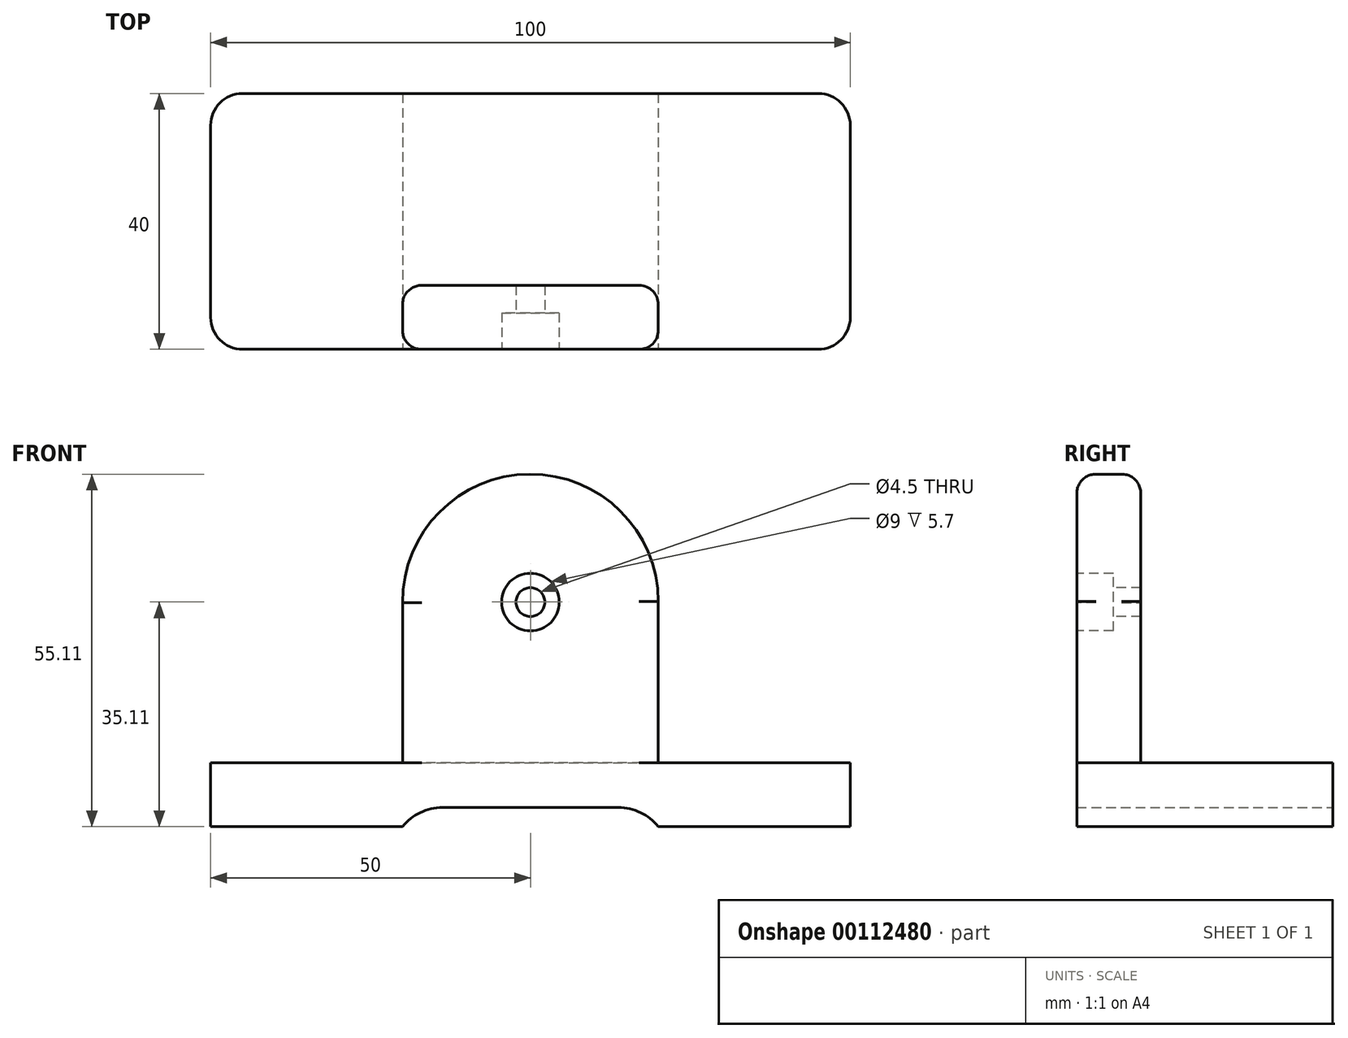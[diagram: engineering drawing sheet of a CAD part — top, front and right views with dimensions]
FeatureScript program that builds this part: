
annotation { "Feature Type Name" : "Feature", "Feature Type Description" : "" }
export const myFeature = defineFeature(function(context is Context, id is Id, definition is map)
    precondition{}
    {
        {
            var Q0;
            Q0=qCreatedBy(makeId("Top.planeOp"),FACE);
            var sketch = newSketch(context, id + "F0", { "sketchPlane" : qUnion([Q0])});
            skLineSegment(sketch, "E0.bottom", {"start": v(0, 0) * mm, "end": v(-100, 0) * mm});
            skLineSegment(sketch, "E0.top", {"start": v(0, 40) * mm, "end": v(-100, 40) * mm});
            skLineSegment(sketch, "E0.left", {"start": v(0, 0) * mm, "end": v(0, 40) * mm});
            skLineSegment(sketch, "E0.right", {"start": v(-100, 0) * mm, "end": v(-100, 40) * mm});
            skSolve(sketch);
        }
        {
            var Q0;
            Q0 = qSketchRegion(id + "F0", true);
            var Q1;
            Q1 = qSketchRegion(id + "F2", true);
            extrude(context, id + "F1", {"entities" : qUnion([Q0, Q1]), "depth" : 10 * mm});
        }
        {
            var Q0;
            Q0=qCreatedBy(makeId("Front.planeOp"),FACE);
            var sketch = newSketch(context, id + "F2", { "sketchPlane" : qUnion([Q0])});
            skLineSegment(sketch, "E1", {"start": v(-70, 35) * mm, "end": v(-70, 0) * mm});
            skLineSegment(sketch, "E2", {"start": v(-30, 0) * mm, "end": v(-30, 35.22) * mm});
            skArc(sketch, "E3", {"start": v(-30, 35.22) * mm, "mid": v(-50.1, 55.1) * mm, "end": v(-70, 35) * mm});
            skLineSegment(sketch, "E4", {"start": v(-70, 0) * mm, "end": v(-30, 0) * mm});
            skSolve(sketch);
        }
        {
            var Q0;
            Q0=makeQuery(id+"F2.imprint","IMPRINT",FACE,{"disambiguationData":[TD([[makeQuery(id+"F2.imprint","IMPRINT",EDGE,{"derivedFrom":sQuery(id+"F2.wireOp",EDGE,"E1")}),1.0]])]});
            extrude(context, id + "F3", {"entities" : qUnion([Q0]), "operationType" : NewBodyOperationType.ADD, "oppositeDirection" : true, "depth" : 10 * mm});
        }
        {
            var Q0;
            Q0=makeQuery(id+"F3.boolean.opBoolean","MERGE",FACE,{"derivedFrom":[makeQuery(id+"F1.opExtrude","SWEPT_FACE",FACE,{"disambiguationData":[OSD([sQuery(id+"F0.wireOp",EDGE,"E0.bottom")])]}),makeQuery(id+"F3.opExtrude","CAP_FACE",FACE,{"disambiguationData":[OSD([sQuery(id+"F2.wireOp",EDGE,"E1"),sQuery(id+"F2.wireOp",EDGE,"E2"),sQuery(id+"F2.wireOp",EDGE,"E3"),sQuery(id+"F2.wireOp",EDGE,"E4")])],"isStart":true})]});
            var sketch = newSketch(context, id + "F4", { "sketchPlane" : qUnion([Q0])});
            skLineSegment(sketch, "E5.bottom", {"start": v(-70, 0) * mm, "end": v(-30, 0) * mm});
            skLineSegment(sketch, "E5.top", {"start": v(-70, 3) * mm, "end": v(-30, 3) * mm});
            skLineSegment(sketch, "E5.left", {"start": v(-70, 0) * mm, "end": v(-70, 3) * mm});
            skLineSegment(sketch, "E5.right", {"start": v(-30, 0) * mm, "end": v(-30, 3) * mm});
            skSolve(sketch);
        }
        {
            var Q0;
            Q0 = qSketchRegion(id + "F4", true);
            extrude(context, id + "F5", {"entities" : qUnion([Q0]), "operationType" : NewBodyOperationType.REMOVE, "endBound" : BoundingType.THROUGH_ALL, "oppositeDirection" : true, "depth" : 25 * mm});
        }
        {
            var Q0;
            Q0=makeQuery(id+"F3.boolean.opBoolean","MERGE",FACE,{"derivedFrom":[makeQuery(id+"F1.opExtrude","SWEPT_FACE",FACE,{"disambiguationData":[OSD([sQuery(id+"F0.wireOp",EDGE,"E0.bottom")])]}),makeQuery(id+"F3.opExtrude","CAP_FACE",FACE,{"disambiguationData":[OSD([sQuery(id+"F2.wireOp",EDGE,"E1"),sQuery(id+"F2.wireOp",EDGE,"E2"),sQuery(id+"F2.wireOp",EDGE,"E3"),sQuery(id+"F2.wireOp",EDGE,"E4")])],"isStart":true})]});
            var sketch = newSketch(context, id + "F6", { "sketchPlane" : qUnion([Q0])});
            skCircle(sketch, "E6", {"center": v(-50, 35.1) * mm, "radius": 2.25 * mm});
            skSolve(sketch);
        }
        {
            var Q0;
            Q0 = qSketchRegion(id + "F6", true);
            extrude(context, id + "F7", {"entities" : qUnion([Q0]), "operationType" : NewBodyOperationType.REMOVE, "endBound" : BoundingType.THROUGH_ALL, "oppositeDirection" : true, "depth" : 25 * mm});
        }
        {
            var Q0;
            Q0=makeQuery(id+"F3.boolean.opBoolean","MERGE",FACE,{"derivedFrom":[makeQuery(id+"F1.opExtrude","SWEPT_FACE",FACE,{"disambiguationData":[OSD([sQuery(id+"F0.wireOp",EDGE,"E0.bottom")])]}),makeQuery(id+"F3.opExtrude","CAP_FACE",FACE,{"disambiguationData":[OSD([sQuery(id+"F2.wireOp",EDGE,"E1"),sQuery(id+"F2.wireOp",EDGE,"E2"),sQuery(id+"F2.wireOp",EDGE,"E3"),sQuery(id+"F2.wireOp",EDGE,"E4")])],"isStart":true})]});
            var sketch = newSketch(context, id + "F8", { "sketchPlane" : qUnion([Q0])});
            skPoint(sketch, "E7.centerSnap0", {"position": v(-50.1, 55.1) * mm});
            skCircle(sketch, "E8", {"center": v(-50, 35.1) * mm, "radius": 4.5 * mm});
            skSolve(sketch);
        }
        {
            var Q0;
            Q0=makeQuery(id+"F3.opExtrude","CAP_EDGE",EDGE,{"disambiguationData":[OSD([sQuery(id+"F2.wireOp",EDGE,"E1")])],"isStart":true});
            var Q1;
            Q1=makeQuery(id+"F3.opExtrude","CAP_EDGE",EDGE,{"disambiguationData":[OSD([sQuery(id+"F2.wireOp",EDGE,"E2")])],"isStart":true});
            var Q2;
            Q2=makeQuery(id+"F3.opExtrude","CAP_EDGE",EDGE,{"disambiguationData":[OSD([sQuery(id+"F2.wireOp",EDGE,"E3")])],"isStart":true});
            fillet(context, id + "F9", {"entities" : qUnion([Q0, Q1, Q2]), "radius" : 3 * mm, "tangentPropagation" : true, "allowEdgeOverflow" : false});
        }
        {
            var Q0;
            Q0=makeQuery(id+"F3.opExtrude","CAP_EDGE",EDGE,{"disambiguationData":[OSD([sQuery(id+"F2.wireOp",EDGE,"E2")])],"isStart":false});
            var Q1;
            Q1=makeQuery(id+"F3.opExtrude","CAP_EDGE",EDGE,{"disambiguationData":[OSD([sQuery(id+"F2.wireOp",EDGE,"E1")])],"isStart":false});
            var Q2;
            Q2=makeQuery(id+"F3.opExtrude","CAP_EDGE",EDGE,{"disambiguationData":[OSD([sQuery(id+"F2.wireOp",EDGE,"E3")])],"isStart":false});
            fillet(context, id + "F10", {"entities" : qUnion([Q0, Q1, Q2]), "radius" : 3 * mm, "tangentPropagation" : true, "allowEdgeOverflow" : false});
        }
        {
            var Q0;
            Q0 = qSketchRegion(id + "F8", true);
            extrude(context, id + "F11", {"entities" : qUnion([Q0]), "operationType" : NewBodyOperationType.REMOVE, "oppositeDirection" : true, "depth" : 5.7 * mm});
        }
        {
            var Q0;
            Q0=makeQuery(id+"F5.boolean.opBoolean","COPY",EDGE,{"derivedFrom":makeQuery(id+"F5.opExtrude","SWEPT_EDGE",EDGE,{"disambiguationData":[OSD([sQuery(id+"F4.wireOp",EDGE,"E5.top"),sQuery(id+"F4.wireOp",EDGE,"E5.left")])]})});
            var Q1;
            Q1=makeQuery(id+"F5.boolean.opBoolean","COPY",EDGE,{"derivedFrom":makeQuery(id+"F5.opExtrude","SWEPT_EDGE",EDGE,{"disambiguationData":[OSD([sQuery(id+"F4.wireOp",EDGE,"E5.top"),sQuery(id+"F4.wireOp",EDGE,"E5.right")])]})});
            fillet(context, id + "F12", {"entities" : qUnion([Q0, Q1]), "radius" : 8 * mm, "tangentPropagation" : true, "allowEdgeOverflow" : false});
        }
        {
            var Q0;
            Q0=makeQuery(id+"F1.opExtrude","SWEPT_EDGE",EDGE,{"disambiguationData":[OSD([sQuery(id+"F0.wireOp",EDGE,"E0.bottom"),sQuery(id+"F0.wireOp",EDGE,"E0.right")])]});
            var Q1;
            Q1=makeQuery(id+"F1.opExtrude","SWEPT_EDGE",EDGE,{"disambiguationData":[OSD([sQuery(id+"F0.wireOp",EDGE,"E0.top"),sQuery(id+"F0.wireOp",EDGE,"E0.right")])]});
            var Q2;
            Q2=makeQuery(id+"F1.opExtrude","SWEPT_EDGE",EDGE,{"disambiguationData":[OSD([sQuery(id+"F0.wireOp",EDGE,"E0.bottom"),sQuery(id+"F0.wireOp",EDGE,"E0.left")])]});
            var Q3;
            Q3=makeQuery(id+"F1.opExtrude","SWEPT_EDGE",EDGE,{"disambiguationData":[OSD([sQuery(id+"F0.wireOp",EDGE,"E0.top"),sQuery(id+"F0.wireOp",EDGE,"E0.left")])]});
            fillet(context, id + "F13", {"entities" : qUnion([Q0, Q1, Q2, Q3]), "radius" : 5 * mm, "tangentPropagation" : true, "allowEdgeOverflow" : false});
        }
    });
